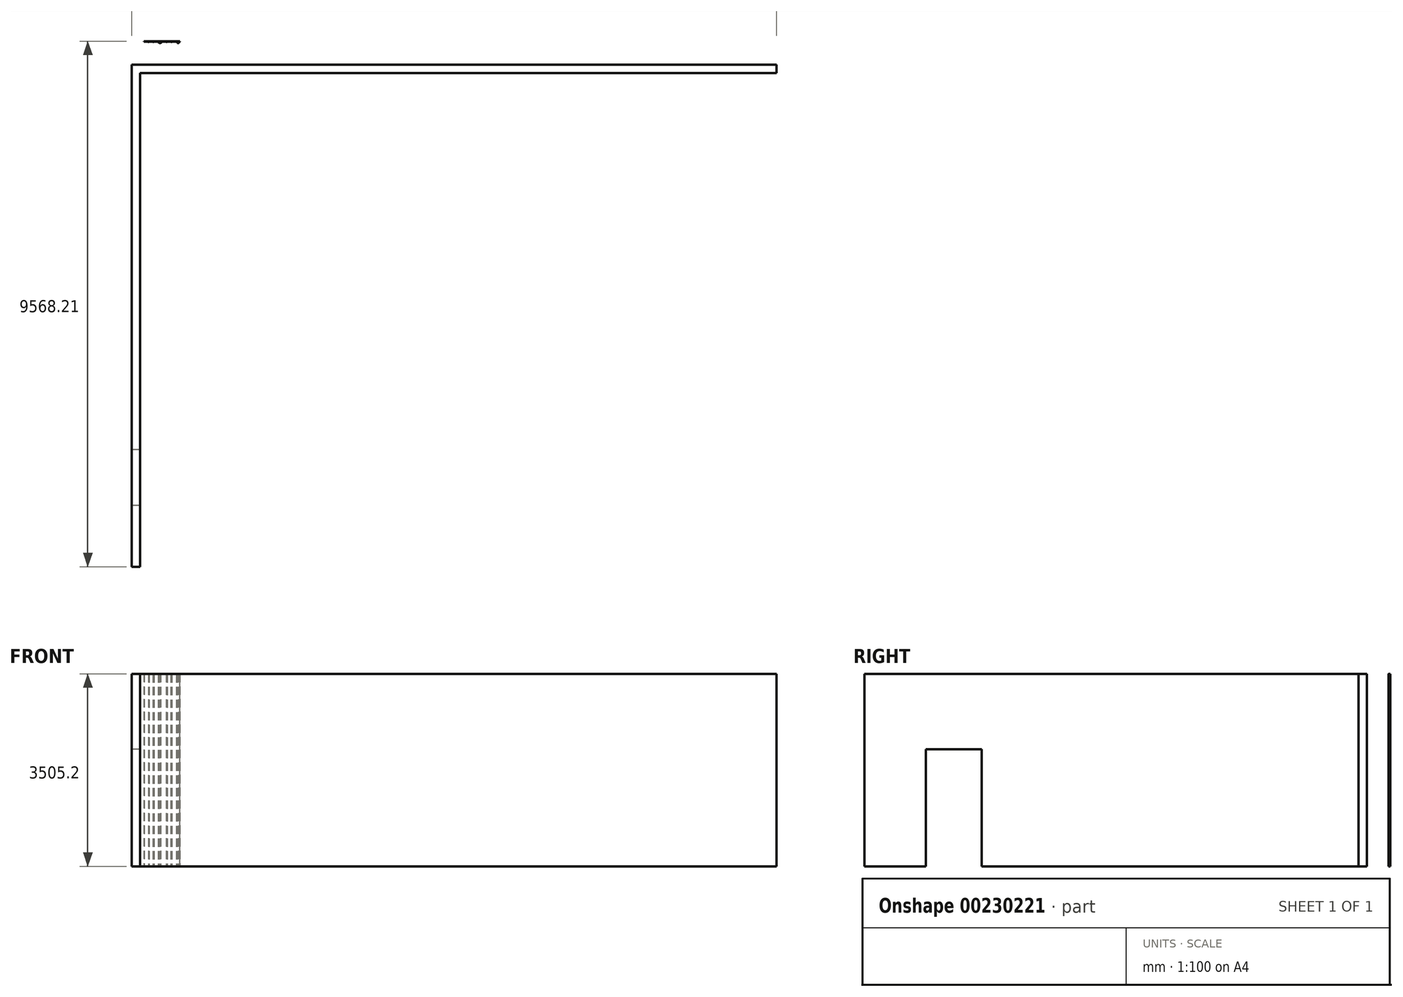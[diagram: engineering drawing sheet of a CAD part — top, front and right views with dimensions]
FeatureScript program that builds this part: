
annotation { "Feature Type Name" : "Feature", "Feature Type Description" : "" }
export const myFeature = defineFeature(function(context is Context, id is Id, definition is map)
    precondition{}
    {
        {
            var Q0;
            Q0=qCreatedBy(makeId("Top.planeOp"),FACE);
            var sketch = newSketch(context, id + "F0", { "sketchPlane" : qUnion([Q0])});
            skLineSegment(sketch, "E0.bottom", {"start": v(0, 0) * mm, "end": v(152.4, 0) * mm});
            skLineSegment(sketch, "E0.top", {"start": v(0, 9144) * mm, "end": v(152.4, 9144) * mm});
            skLineSegment(sketch, "E0.left", {"start": v(0, 0) * mm, "end": v(0, 9144) * mm});
            skLineSegment(sketch, "E0.right", {"start": v(152.4, 0) * mm, "end": v(152.4, 8991.6) * mm});
            skLineSegment(sketch, "E1.bottom", {"start": v(0, 9144) * mm, "end": v(11734.8, 9144) * mm});
            skLineSegment(sketch, "E1.top", {"start": v(152.4, 8991.6) * mm, "end": v(11734.8, 8991.6) * mm});
            skLineSegment(sketch, "E1.left", {"start": v(0, 9144) * mm, "end": v(0, 8991.6) * mm});
            skLineSegment(sketch, "E1.right", {"start": v(11734.8, 9144) * mm, "end": v(11734.8, 8991.6) * mm});
            skSolve(sketch);
        }
        {
            var Q0;
            Q0 = qSketchRegion(id + "F0", true);
            extrude(context, id + "F1", {"entities" : qUnion([Q0]), "depth" : 3505.2 * mm});
        }
        {
            var Q0;
            Q0=makeQuery(id+"F1.opExtrude","SWEPT_FACE",FACE,{"disambiguationData":[OSD([sQuery(id+"F0.wireOp",EDGE,"E0.left"),sQuery(id+"F0.wireOp",EDGE,"E1.left")])]});
            var sketch = newSketch(context, id + "F2", { "sketchPlane" : qUnion([Q0])});
            skLineSegment(sketch, "E2", {"start": v(-9144, 0) * mm, "end": v(-2133.6, 0) * mm});
            skLineSegment(sketch, "E3", {"start": v(-2133.6, 0) * mm, "end": v(-2133.6, 2133.6) * mm});
            skLineSegment(sketch, "E4", {"start": v(-2133.6, 2133.6) * mm, "end": v(-1117.6, 2133.6) * mm});
            skLineSegment(sketch, "E5", {"start": v(-1117.6, 2133.6) * mm, "end": v(-1117.6, 0) * mm});
            skLineSegment(sketch, "E6", {"start": v(-1117.6, 0) * mm, "end": v(-2133.6, 0) * mm});
            skSolve(sketch);
        }
        {
            var Q0;
            Q0 = qSketchRegion(id + "F2", true);
            extrude(context, id + "F3", {"entities" : qUnion([Q0]), "operationType" : NewBodyOperationType.REMOVE, "oppositeDirection" : true, "depth" : 203.2 * mm});
        }
        {
            var Q0;
            Q0=qCreatedBy(makeId("Top.planeOp"),FACE);
            var sketch = newSketch(context, id + "F4", { "sketchPlane" : qUnion([Q0])});
            skLineSegment(sketch, "E7", {"start": v(221.45, 9561.86) * mm, "end": v(291.3, 9561.86) * mm});
            skLineSegment(sketch, "E8", {"start": v(551.65, 9561.86) * mm, "end": v(621.5, 9561.86) * mm});
            skLineSegment(sketch, "E9", {"start": v(851.57, 9537.39) * mm, "end": v(831.43, 9537.39) * mm});
            skLineSegment(sketch, "E10", {"start": v(524.93, 9536.46) * mm, "end": v(502.16, 9536.46) * mm});
            skLineSegment(sketch, "E11", {"start": v(499.92, 9537.39) * mm, "end": v(475.45, 9561.86) * mm});
            skLineSegment(sketch, "E12", {"start": v(527.18, 9537.39) * mm, "end": v(551.65, 9561.86) * mm});
            skLineSegment(sketch, "E13", {"start": v(829.19, 9538.32) * mm, "end": v(805.65, 9561.86) * mm});
            skLineSegment(sketch, "E14", {"start": v(853.82, 9538.32) * mm, "end": v(877.36, 9561.86) * mm});
            skLineSegment(sketch, "E15", {"start": v(805.65, 9561.86) * mm, "end": v(731.3, 9561.86) * mm});
            skLineSegment(sketch, "E16", {"start": v(710.4, 9561.86) * mm, "end": v(646.9, 9561.86) * mm});
            skLineSegment(sketch, "E17", {"start": v(475.45, 9561.86) * mm, "end": v(405.6, 9561.86) * mm});
            skLineSegment(sketch, "E18", {"start": v(380.2, 9561.86) * mm, "end": v(316.7, 9561.86) * mm});
            skLineSegment(sketch, "E19", {"start": v(298.96, 9555.5) * mm, "end": v(309.03, 9555.5) * mm});
            skLineSegment(sketch, "E20", {"start": v(397.93, 9555.5) * mm, "end": v(387.86, 9555.5) * mm});
            skLineSegment(sketch, "E21", {"start": v(639.23, 9555.5) * mm, "end": v(629.16, 9555.5) * mm});
            skLineSegment(sketch, "E22", {"start": v(724.57, 9556.44) * mm, "end": v(717.13, 9556.44) * mm});
            skLineSegment(sketch, "E23", {"start": v(731.3, 9561.86) * mm, "end": v(726.82, 9557.37) * mm});
            skLineSegment(sketch, "E24", {"start": v(710.4, 9561.86) * mm, "end": v(714.89, 9557.37) * mm});
            skLineSegment(sketch, "E25", {"start": v(646.9, 9561.86) * mm, "end": v(641.48, 9556.44) * mm});
            skLineSegment(sketch, "E26", {"start": v(621.5, 9561.86) * mm, "end": v(626.92, 9556.44) * mm});
            skLineSegment(sketch, "E27", {"start": v(405.6, 9561.86) * mm, "end": v(400.18, 9556.44) * mm});
            skLineSegment(sketch, "E28", {"start": v(380.2, 9561.86) * mm, "end": v(385.62, 9556.44) * mm});
            skLineSegment(sketch, "E29", {"start": v(316.7, 9561.86) * mm, "end": v(311.28, 9556.44) * mm});
            skLineSegment(sketch, "E30", {"start": v(291.3, 9561.86) * mm, "end": v(296.72, 9556.44) * mm});
            skLineSegment(sketch, "E31", {"start": v(221.45, 9561.86) * mm, "end": v(221.45, 9568.2) * mm});
            skLineSegment(sketch, "E32", {"start": v(221.45, 9568.2) * mm, "end": v(877.36, 9568.2) * mm});
            skLineSegment(sketch, "E33", {"start": v(877.36, 9568.2) * mm, "end": v(877.36, 9561.86) * mm});
            skLineSegment(sketch, "E34.trimOffspring", {"start": v(731.3, 9561.86) * mm, "end": v(805.65, 9561.86) * mm});
            skLineSegment(sketch, "E35.trimOffspring", {"start": v(646.9, 9561.86) * mm, "end": v(710.4, 9561.86) * mm});
            skLineSegment(sketch, "E36.trimOffspring", {"start": v(405.6, 9561.86) * mm, "end": v(475.45, 9561.86) * mm});
            skLineSegment(sketch, "E37.trimOffspring", {"start": v(316.7, 9561.86) * mm, "end": v(380.2, 9561.86) * mm});
            skPoint(sketch, "E38.visualSharp", {"position": v(852.89, 9537.39) * mm});
            skArc(sketch, "E38.filletArc", {"start": v(851.57, 9537.39) * mm, "mid": v(852.79, 9537.63) * mm, "end": v(853.82, 9538.32) * mm});
            skPoint(sketch, "E39.visualSharp", {"position": v(830.12, 9537.39) * mm});
            skArc(sketch, "E39.filletArc", {"start": v(829.19, 9538.32) * mm, "mid": v(830.22, 9537.63) * mm, "end": v(831.43, 9537.39) * mm});
            skPoint(sketch, "E40.visualSharp", {"position": v(725.89, 9556.44) * mm});
            skArc(sketch, "E40.filletArc", {"start": v(724.57, 9556.44) * mm, "mid": v(725.79, 9556.68) * mm, "end": v(726.82, 9557.37) * mm});
            skPoint(sketch, "E41.visualSharp", {"position": v(715.82, 9556.44) * mm});
            skArc(sketch, "E41.filletArc", {"start": v(714.89, 9557.37) * mm, "mid": v(715.92, 9556.68) * mm, "end": v(717.13, 9556.44) * mm});
            skPoint(sketch, "E42.visualSharp", {"position": v(640.55, 9555.5) * mm});
            skArc(sketch, "E42.filletArc", {"start": v(639.23, 9555.5) * mm, "mid": v(640.45, 9555.75) * mm, "end": v(641.48, 9556.44) * mm});
            skPoint(sketch, "E43.visualSharp", {"position": v(627.85, 9555.5) * mm});
            skArc(sketch, "E43.filletArc", {"start": v(626.92, 9556.44) * mm, "mid": v(627.95, 9555.75) * mm, "end": v(629.16, 9555.5) * mm});
            skPoint(sketch, "E44.visualSharp", {"position": v(526.25, 9536.46) * mm});
            skArc(sketch, "E44.filletArc", {"start": v(524.93, 9536.46) * mm, "mid": v(526.15, 9536.7) * mm, "end": v(527.18, 9537.39) * mm});
            skPoint(sketch, "E45.visualSharp", {"position": v(500.85, 9536.46) * mm});
            skArc(sketch, "E45.filletArc", {"start": v(499.92, 9537.39) * mm, "mid": v(500.95, 9536.7) * mm, "end": v(502.16, 9536.46) * mm});
            skPoint(sketch, "E46.visualSharp", {"position": v(399.25, 9555.5) * mm});
            skArc(sketch, "E46.filletArc", {"start": v(397.93, 9555.5) * mm, "mid": v(399.15, 9555.75) * mm, "end": v(400.18, 9556.44) * mm});
            skPoint(sketch, "E47.visualSharp", {"position": v(386.55, 9555.5) * mm});
            skArc(sketch, "E47.filletArc", {"start": v(385.62, 9556.44) * mm, "mid": v(386.65, 9555.75) * mm, "end": v(387.86, 9555.5) * mm});
            skPoint(sketch, "E48.visualSharp", {"position": v(310.35, 9555.5) * mm});
            skArc(sketch, "E48.filletArc", {"start": v(309.03, 9555.5) * mm, "mid": v(310.25, 9555.75) * mm, "end": v(311.28, 9556.44) * mm});
            skPoint(sketch, "E49.visualSharp", {"position": v(297.65, 9555.5) * mm});
            skArc(sketch, "E49.filletArc", {"start": v(296.72, 9556.44) * mm, "mid": v(297.75, 9555.75) * mm, "end": v(298.96, 9555.5) * mm});
            skSolve(sketch);
        }
        {
            var Q0;
            Q0=makeQuery(id+"F4.imprint","IMPRINT",FACE,{"disambiguationData":[TD([[makeQuery(id+"F4.imprint","IMPRINT",EDGE,{"derivedFrom":sQuery(id+"F4.wireOp",EDGE,"E7")}),1.0]])]});
            extrude(context, id + "F5", {"entities" : qUnion([Q0]), "depth" : 3505.2 * mm});
        }
        {
            var Q0;
            Q0=makeQuery(id+"F5.opExtrude","SWEPT_FACE",FACE,{"disambiguationData":[OSD([sQuery(id+"F4.wireOp",EDGE,"E32")])]});
            shell(context, id + "F6", {"entities" : qUnion([Q0]), "thickness" : 4.78 * mm});
        }
        {
            var Q0;
            Q0=makeQuery(id+"F5.opExtrude","SWEPT_EDGE",EDGE,{"disambiguationData":[OSD([sQuery(id+"F4.wireOp",EDGE,"E13"),sQuery(id+"F4.wireOp",EDGE,"E34.trimOffspring")])]});
            var Q1;
            Q1=makeQuery(id+"F5.opExtrude","SWEPT_EDGE",EDGE,{"disambiguationData":[OSD([sQuery(id+"F4.wireOp",EDGE,"E23"),sQuery(id+"F4.wireOp",EDGE,"E34.trimOffspring")])]});
            var Q2;
            Q2=makeQuery(id+"F5.opExtrude","SWEPT_EDGE",EDGE,{"disambiguationData":[OSD([sQuery(id+"F4.wireOp",EDGE,"E24"),sQuery(id+"F4.wireOp",EDGE,"E35.trimOffspring")])]});
            var Q3;
            Q3=makeQuery(id+"F5.opExtrude","SWEPT_EDGE",EDGE,{"disambiguationData":[OSD([sQuery(id+"F4.wireOp",EDGE,"E25"),sQuery(id+"F4.wireOp",EDGE,"E35.trimOffspring")])]});
            var Q4;
            Q4=makeQuery(id+"F5.opExtrude","SWEPT_EDGE",EDGE,{"disambiguationData":[OSD([sQuery(id+"F4.wireOp",EDGE,"E8"),sQuery(id+"F4.wireOp",EDGE,"E26")])]});
            var Q5;
            Q5=makeQuery(id+"F5.opExtrude","SWEPT_EDGE",EDGE,{"disambiguationData":[OSD([sQuery(id+"F4.wireOp",EDGE,"E8"),sQuery(id+"F4.wireOp",EDGE,"E12")])]});
            var Q6;
            Q6=makeQuery(id+"F5.opExtrude","SWEPT_EDGE",EDGE,{"disambiguationData":[OSD([sQuery(id+"F4.wireOp",EDGE,"E11"),sQuery(id+"F4.wireOp",EDGE,"E36.trimOffspring")])]});
            var Q7;
            Q7=makeQuery(id+"F5.opExtrude","SWEPT_EDGE",EDGE,{"disambiguationData":[OSD([sQuery(id+"F4.wireOp",EDGE,"E27"),sQuery(id+"F4.wireOp",EDGE,"E36.trimOffspring")])]});
            var Q8;
            Q8=makeQuery(id+"F5.opExtrude","SWEPT_EDGE",EDGE,{"disambiguationData":[OSD([sQuery(id+"F4.wireOp",EDGE,"E28"),sQuery(id+"F4.wireOp",EDGE,"E37.trimOffspring")])]});
            var Q9;
            Q9=makeQuery(id+"F5.opExtrude","SWEPT_EDGE",EDGE,{"disambiguationData":[OSD([sQuery(id+"F4.wireOp",EDGE,"E29"),sQuery(id+"F4.wireOp",EDGE,"E37.trimOffspring")])]});
            var Q10;
            Q10=makeQuery(id+"F5.opExtrude","SWEPT_EDGE",EDGE,{"disambiguationData":[OSD([sQuery(id+"F4.wireOp",EDGE,"E7"),sQuery(id+"F4.wireOp",EDGE,"E30")])]});
            fillet(context, id + "F7", {"entities" : qUnion([Q0, Q1, Q2, Q3, Q4, Q5, Q6, Q7, Q8, Q9, Q10]), "radius" : 3.17 * mm, "tangentPropagation" : true, "allowEdgeOverflow" : false});
        }
        {
            var Q0;
            Q0=makeQuery(id+"F6.opShell","OFFSET_EDGE",EDGE,{"disambiguationData":[OSD([sQuery(id+"F4.wireOp",EDGE,"E29"),sQuery(id+"F4.wireOp",EDGE,"E37.trimOffspring")])]});
            var Q1;
            Q1=makeQuery(id+"F6.opShell","OFFSET_EDGE",EDGE,{"disambiguationData":[OSD([sQuery(id+"F4.wireOp",EDGE,"E7"),sQuery(id+"F4.wireOp",EDGE,"E30")])]});
            var Q2;
            Q2=makeQuery(id+"F6.opShell","OFFSET_EDGE",EDGE,{"disambiguationData":[OSD([sQuery(id+"F4.wireOp",EDGE,"E28"),sQuery(id+"F4.wireOp",EDGE,"E37.trimOffspring")])]});
            var Q3;
            Q3=makeQuery(id+"F6.opShell","OFFSET_EDGE",EDGE,{"disambiguationData":[OSD([sQuery(id+"F4.wireOp",EDGE,"E27"),sQuery(id+"F4.wireOp",EDGE,"E36.trimOffspring")])]});
            var Q4;
            Q4=makeQuery(id+"F6.opShell","OFFSET_EDGE",EDGE,{"disambiguationData":[OSD([sQuery(id+"F4.wireOp",EDGE,"E11"),sQuery(id+"F4.wireOp",EDGE,"E36.trimOffspring")])]});
            var Q5;
            Q5=makeQuery(id+"F6.opShell","OFFSET_EDGE",EDGE,{"disambiguationData":[OSD([sQuery(id+"F4.wireOp",EDGE,"E8"),sQuery(id+"F4.wireOp",EDGE,"E12")])]});
            var Q6;
            Q6=makeQuery(id+"F6.opShell","OFFSET_EDGE",EDGE,{"disambiguationData":[OSD([sQuery(id+"F4.wireOp",EDGE,"E8"),sQuery(id+"F4.wireOp",EDGE,"E26")])]});
            var Q7;
            Q7=makeQuery(id+"F6.opShell","OFFSET_EDGE",EDGE,{"disambiguationData":[OSD([sQuery(id+"F4.wireOp",EDGE,"E25"),sQuery(id+"F4.wireOp",EDGE,"E35.trimOffspring")])]});
            var Q8;
            Q8=makeQuery(id+"F6.opShell","OFFSET_EDGE",EDGE,{"disambiguationData":[OSD([sQuery(id+"F4.wireOp",EDGE,"E24"),sQuery(id+"F4.wireOp",EDGE,"E35.trimOffspring")])]});
            var Q9;
            Q9=makeQuery(id+"F6.opShell","OFFSET_EDGE",EDGE,{"disambiguationData":[OSD([sQuery(id+"F4.wireOp",EDGE,"E23"),sQuery(id+"F4.wireOp",EDGE,"E34.trimOffspring")])]});
            var Q10;
            Q10=makeQuery(id+"F6.opShell","OFFSET_EDGE",EDGE,{"disambiguationData":[OSD([sQuery(id+"F4.wireOp",EDGE,"E13"),sQuery(id+"F4.wireOp",EDGE,"E34.trimOffspring")])]});
            var Q11;
            Q11=makeQuery(id+"F6.opShell","OFFSET_EDGE",EDGE,{"disambiguationData":[OSD([sQuery(id+"F4.wireOp",EDGE,"E32"),sQuery(id+"F4.wireOp",EDGE,"E33")])]});
            fillet(context, id + "F8", {"entities" : qUnion([Q0, Q1, Q2, Q3, Q4, Q5, Q6, Q7, Q8, Q9, Q10, Q11]), "radius" : 5.08 * mm, "tangentPropagation" : true, "allowEdgeOverflow" : false});
        }
    });
